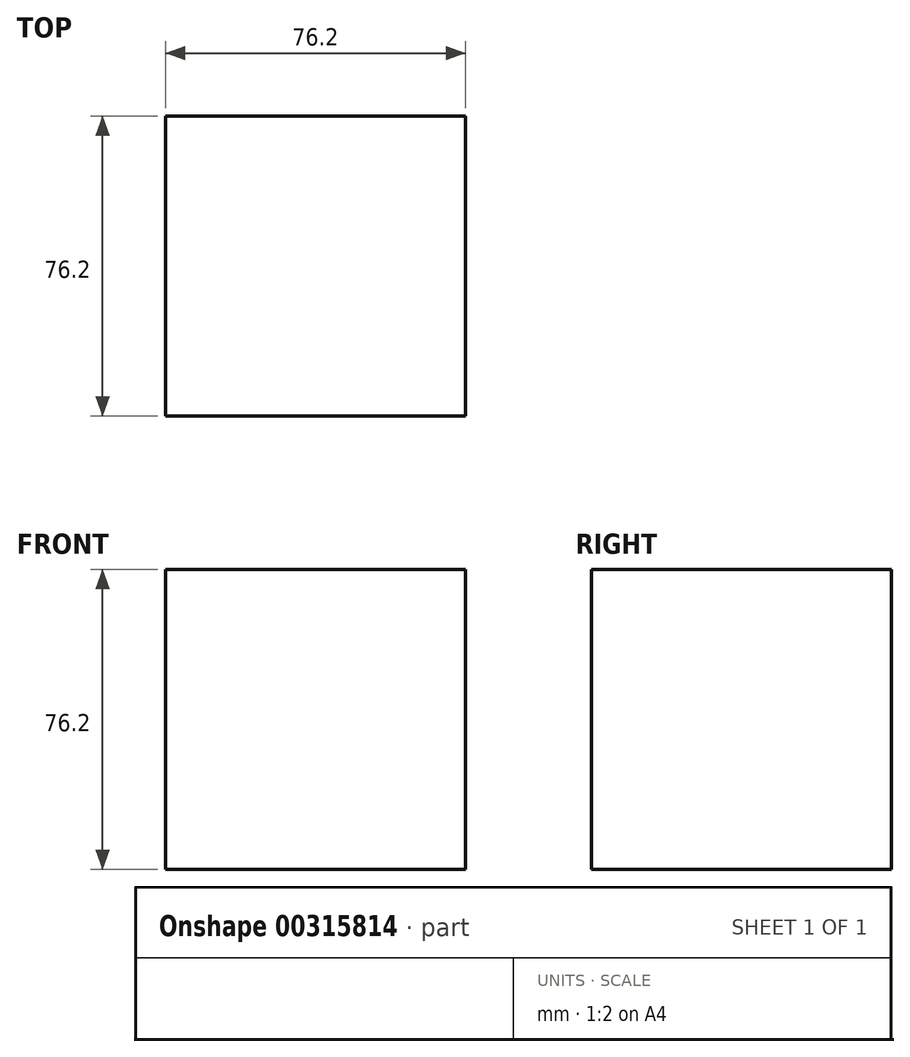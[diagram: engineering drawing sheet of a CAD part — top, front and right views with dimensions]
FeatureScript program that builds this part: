
annotation { "Feature Type Name" : "Feature", "Feature Type Description" : "" }
export const myFeature = defineFeature(function(context is Context, id is Id, definition is map)
    precondition{}
    {
        {
            var Q0;
            Q0=qCreatedBy(makeId("Front.planeOp"),FACE);
            var sketch = newSketch(context, id + "F0", { "sketchPlane" : qUnion([Q0])});
            skLineSegment(sketch, "E0.bottom", {"start": v(-76.2, -76.2) * mm, "end": v(0, -76.2) * mm});
            skLineSegment(sketch, "E0.top", {"start": v(-76.2, 0) * mm, "end": v(0, 0) * mm});
            skLineSegment(sketch, "E0.left", {"start": v(-76.2, -76.2) * mm, "end": v(-76.2, 0) * mm});
            skLineSegment(sketch, "E0.right", {"start": v(0, -76.2) * mm, "end": v(0, 0) * mm});
            skSolve(sketch);
        }
        {
            var Q0;
            Q0 = qSketchRegion(id + "F0", true);
            extrude(context, id + "F1", {"entities" : qUnion([Q0]), "oppositeDirection" : true, "depth" : 76.2 * mm});
        }
    });
